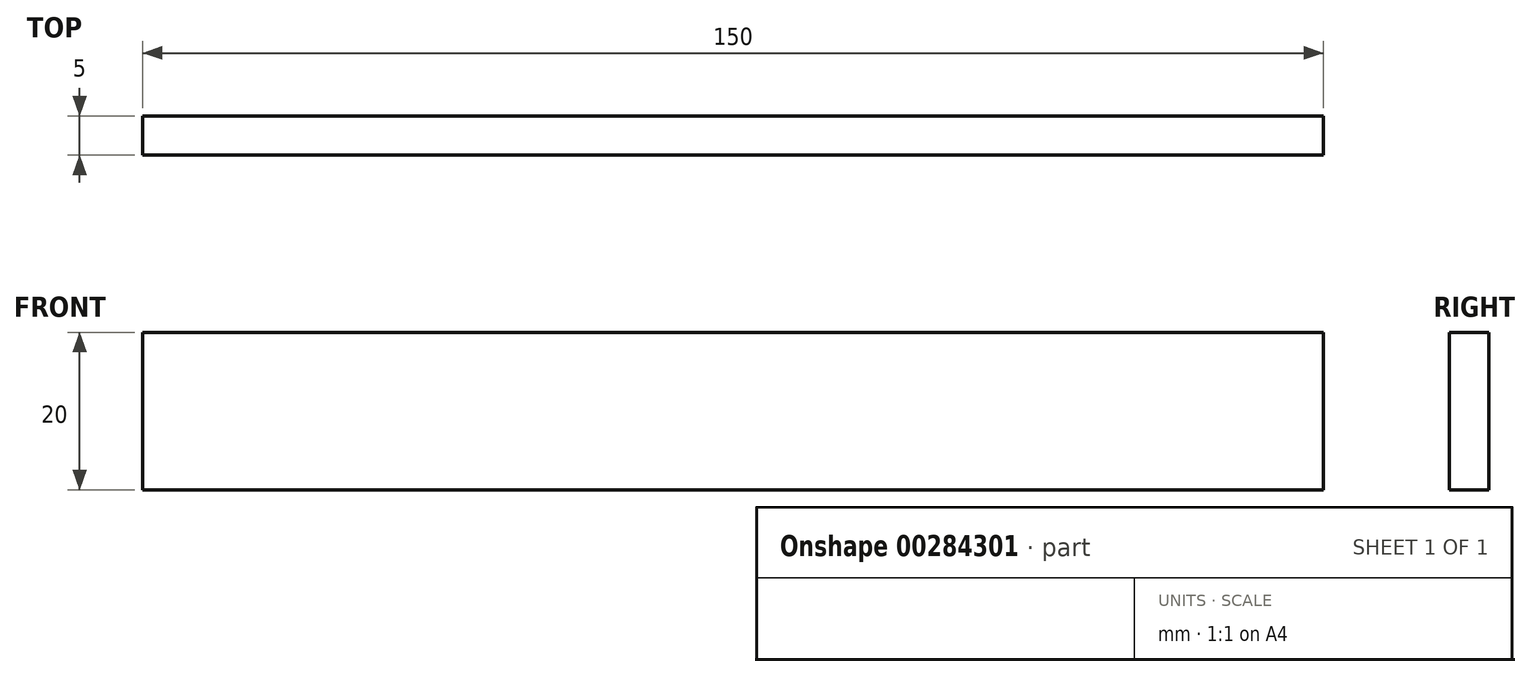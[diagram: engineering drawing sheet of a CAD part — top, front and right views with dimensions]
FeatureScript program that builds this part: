
annotation { "Feature Type Name" : "Feature", "Feature Type Description" : "" }
export const myFeature = defineFeature(function(context is Context, id is Id, definition is map)
    precondition{}
    {
        {
            var Q0;
            Q0=qCreatedBy(makeId("Top.planeOp"),FACE);
            var sketch = newSketch(context, id + "F0", { "sketchPlane" : qUnion([Q0])});
            skLineSegment(sketch, "E0", {"start": v(-67.6, 34.43) * mm, "end": v(82.4, 34.43) * mm});
            skLineSegment(sketch, "E1", {"start": v(-67.6, 34.43) * mm, "end": v(-67.6, 29.43) * mm});
            skLineSegment(sketch, "E2", {"start": v(-67.6, 29.43) * mm, "end": v(82.4, 29.43) * mm});
            skLineSegment(sketch, "E3", {"start": v(82.4, 34.43) * mm, "end": v(82.4, 29.43) * mm});
            skSolve(sketch);
        }
        {
            var Q0;
            Q0=makeQuery(id+"F0.imprint","IMPRINT",FACE,{"disambiguationData":[TD([[makeQuery(id+"F0.imprint","IMPRINT",EDGE,{"derivedFrom":sQuery(id+"F0.wireOp",EDGE,"E0")}),-1.0]])]});
            extrude(context, id + "F1", {"entities" : qUnion([Q0]), "depth" : 20 * mm});
        }
    });
